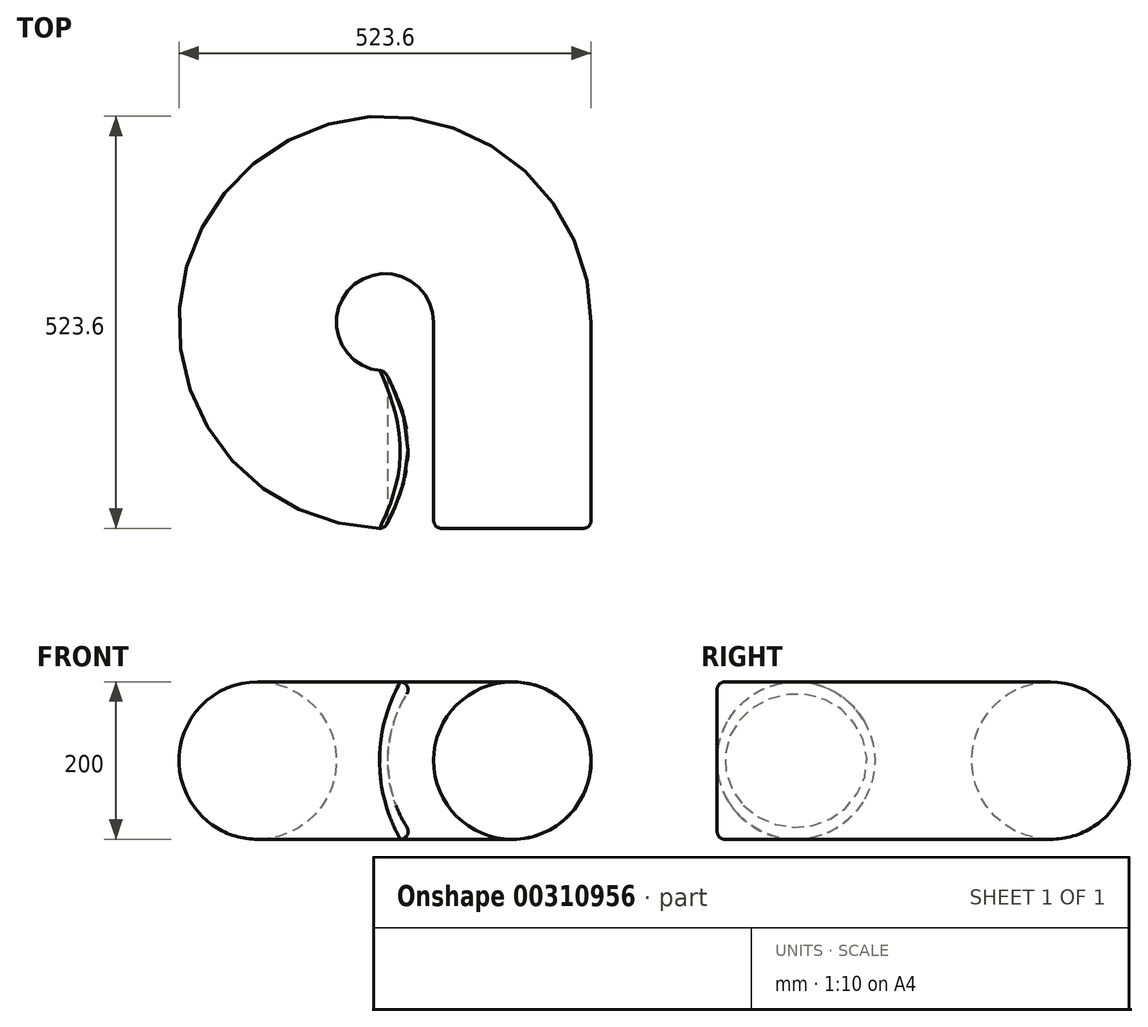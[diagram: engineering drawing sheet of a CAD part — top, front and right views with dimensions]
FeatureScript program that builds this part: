
annotation { "Feature Type Name" : "Feature", "Feature Type Description" : "" }
export const myFeature = defineFeature(function(context is Context, id is Id, definition is map)
    precondition{}
    {
        {
            var Q0;
            Q0=qCreatedBy(makeId("Top.planeOp"),FACE);
            var sketch = newSketch(context, id + "F0", { "sketchPlane" : qUnion([Q0])});
            skArc(sketch, "E0", {"start": v(161.8, 0) * mm, "mid": v(-147.2, 67.15) * mm, "end": v(106.07, -122.18) * mm});
            skLineSegment(sketch, "E1", {"start": v(161.8, 0) * mm, "end": v(161.8, -261.8) * mm});
            skSolve(sketch);
        }
        {
            var Q0;
            Q0=qCreatedBy(makeId("Front.planeOp"),FACE);
            var sketch = newSketch(context, id + "F1", { "sketchPlane" : qUnion([Q0])});
            skCircle(sketch, "E2", {"center": v(161.8, 0) * mm, "radius": 100 * mm});
            skSolve(sketch);
        }
        {
            var Q0;
            Q0=makeQuery(id+"F1.imprint","IMPRINT",FACE,{"disambiguationData":[TD([[makeQuery(id+"F1.imprint","IMPRINT",EDGE,{"derivedFrom":sQuery(id+"F1.wireOp",EDGE,"E2")}),1.0]])]});
            var Q1;
            Q1=sQuery(id+"F0.wireOp",EDGE,"E0");
            sweep(context, id + "F2", {"profiles" : qUnion([Q0]), "path" : qUnion([Q1])});
        }
        {
            var Q0;
            Q0=makeQuery(id+"F2.opSweep","CAP_FACE",FACE,{"disambiguationData":[OSD([sQuery(id+"F0.wireOp",VERTEX,"E0.start"),sQuery(id+"F1.wireOp",EDGE,"E2")])],"isStart":true});
            var Q1;
            Q1=sQuery(id+"F0.wireOp",EDGE,"E1");
            sweep(context, id + "F3", {"operationType" : NewBodyOperationType.ADD, "profiles" : qUnion([Q0]), "path" : qUnion([Q1])});
        }
        {
            var Q0;
            Q0=makeQuery(id+"F3.opSweep","CAP_FACE",FACE,{"disambiguationData":[OSD([sQuery(id+"F0.wireOp",VERTEX,"E0.start"),sQuery(id+"F0.wireOp",VERTEX,"E1.end"),sQuery(id+"F1.wireOp",EDGE,"E2")])],"isStart":false});
            var sketch = newSketch(context, id + "F4", { "sketchPlane" : qUnion([Q0])});
            skCircle(sketch, "E3", {"center": v(161.8, 0) * mm, "radius": 158.54 * mm});
            skCircle(sketch, "E4", {"center": v(161.8, 0) * mm, "radius": 100 * mm});
            skSolve(sketch);
        }
        {
            var Q0;
            Q0=makeQuery(id+"F4.imprint","IMPRINT",FACE,{"disambiguationData":[TD([[makeQuery(id+"F4.imprint","IMPRINT",EDGE,{"derivedFrom":sQuery(id+"F4.wireOp",EDGE,"E3")}),1.0]])]});
            extrude(context, id + "F5", {"entities" : qUnion([Q0]), "operationType" : NewBodyOperationType.REMOVE, "depth" : -261 * mm});
        }
        {
            var Q0;
            Q0=makeQuery(id+"F5.boolean.opBoolean","INTERSECT",EDGE,{"derivedFrom":[makeQuery(id+"F2.opSweep","SWEPT_FACE",FACE,{"disambiguationData":[OSD([sQuery(id+"F0.wireOp",EDGE,"E0"),sQuery(id+"F1.wireOp",EDGE,"E2")])]}),makeQuery(id+"F5.opExtrude","SWEPT_FACE",FACE,{"disambiguationData":[OSD([sQuery(id+"F4.wireOp",EDGE,"E3")])]})]});
            fillet(context, id + "F6", {"entities" : qUnion([Q0]), "radius" : 10 * mm, "tangentPropagation" : true, "allowEdgeOverflow" : false});
        }
        {
            var Q0;
            Q0=makeQuery(id+"F3.opSweep","CAP_EDGE",EDGE,{"disambiguationData":[OSD([sQuery(id+"F0.wireOp",VERTEX,"E0.start"),sQuery(id+"F0.wireOp",VERTEX,"E1.end"),sQuery(id+"F1.wireOp",EDGE,"E2")])],"isStart":false});
            var Q1;
            Q1=makeQuery(id+"F5.boolean.opBoolean","MERGE",FACE,{"derivedFrom":[makeQuery(id+"F3.opSweep","SWEPT_FACE",FACE,{"disambiguationData":[OSD([sQuery(id+"F0.wireOp",VERTEX,"E0.start"),sQuery(id+"F0.wireOp",EDGE,"E1"),sQuery(id+"F1.wireOp",EDGE,"E2")])]}),makeQuery(id+"F5.opExtrude","SWEPT_FACE",FACE,{"disambiguationData":[OSD([sQuery(id+"F4.wireOp",EDGE,"E4")])]})]});
            fillet(context, id + "F7", {"entities" : qUnion([Q0, Q1]), "radius" : 10 * mm, "tangentPropagation" : true, "allowEdgeOverflow" : false});
        }
    });
